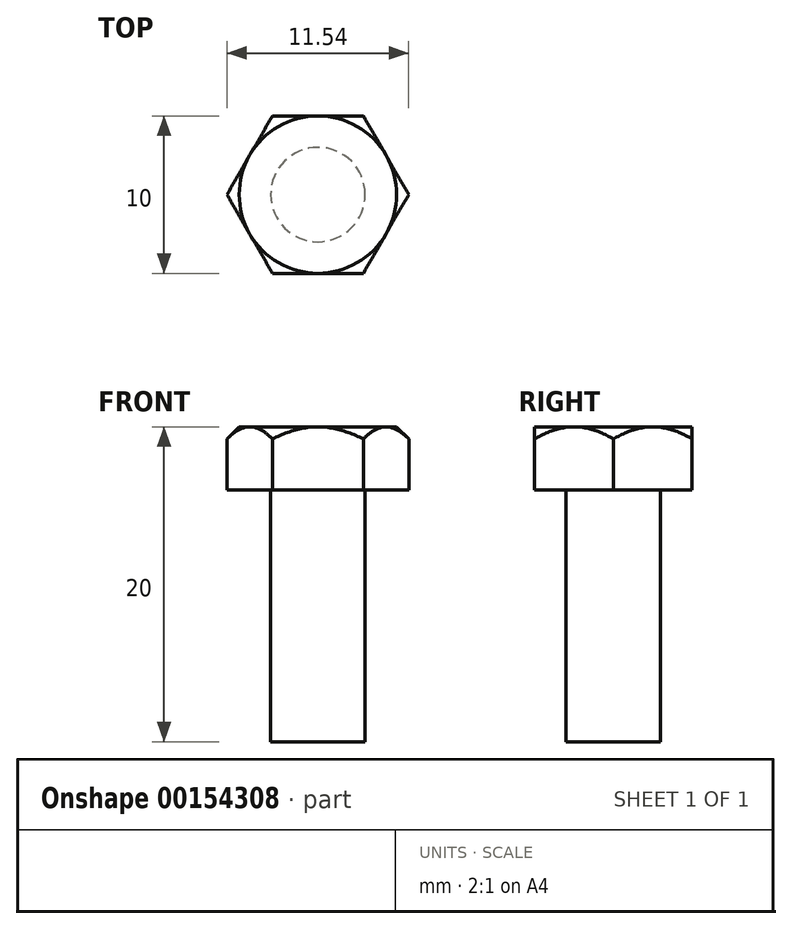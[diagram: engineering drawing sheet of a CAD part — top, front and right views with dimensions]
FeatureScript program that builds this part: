
annotation { "Feature Type Name" : "Feature", "Feature Type Description" : "" }
export const myFeature = defineFeature(function(context is Context, id is Id, definition is map)
    precondition{}
    {
        {
            var Q0;
            Q0=qCreatedBy(makeId("Top.planeOp"),FACE);
            var sketch = newSketch(context, id + "F0", { "sketchPlane" : qUnion([Q0])});
            skCircle(sketch, "E0.cCircle", {"center": v(0, 0) * mm, "radius": 5 * mm, "construction": true});
            skLineSegment(sketch, "E0.0", {"start": v(2.89, -5) * mm, "end": v(-2.89, -5) * mm});
            skLineSegment(sketch, "E0.1", {"start": v(-2.89, -5) * mm, "end": v(-5.77, 0) * mm});
            skLineSegment(sketch, "E0.2", {"start": v(-5.77, 0) * mm, "end": v(-2.89, 5) * mm});
            skLineSegment(sketch, "E0.3", {"start": v(-2.89, 5) * mm, "end": v(2.89, 5) * mm});
            skLineSegment(sketch, "E0.4", {"start": v(2.89, 5) * mm, "end": v(5.77, 0) * mm});
            skLineSegment(sketch, "E0.5", {"start": v(5.77, 0) * mm, "end": v(2.89, -5) * mm});
            skPoint(sketch, "E0.0.midPoint", {"position": v(0, -5) * mm});
            skSolve(sketch);
        }
        {
            var Q0;
            Q0 = qSketchRegion(id + "F0", true);
            extrude(context, id + "F1", {"entities" : qUnion([Q0]), "depth" : 4 * mm});
        }
        {
            var Q0;
            Q0=makeQuery(id+"F1.opExtrude","CAP_FACE",FACE,{"disambiguationData":[OSD([sQuery(id+"F0.wireOp",EDGE,"E0.0"),sQuery(id+"F0.wireOp",EDGE,"E0.1"),sQuery(id+"F0.wireOp",EDGE,"E0.2"),sQuery(id+"F0.wireOp",EDGE,"E0.3"),sQuery(id+"F0.wireOp",EDGE,"E0.4"),sQuery(id+"F0.wireOp",EDGE,"E0.5")])],"isStart":true});
            var sketch = newSketch(context, id + "F2", { "sketchPlane" : qUnion([Q0])});
            skCircle(sketch, "E1", {"center": v(0, 0) * mm, "radius": 3 * mm});
            skSolve(sketch);
        }
        {
            var Q0;
            Q0 = qSketchRegion(id + "F2", true);
            extrude(context, id + "F3", {"entities" : qUnion([Q0]), "operationType" : NewBodyOperationType.ADD, "depth" : 16 * mm});
        }
        {
            var Q0;
            Q0=qCreatedBy(makeId("Right.planeOp"),FACE);
            var sketch = newSketch(context, id + "F4", { "sketchPlane" : qUnion([Q0])});
            skLineSegment(sketch, "E2", {"start": v(5, 4) * mm, "end": v(9, 4) * mm});
            skLineSegment(sketch, "E3", {"start": v(9, 4) * mm, "end": v(9, 0) * mm});
            skLineSegment(sketch, "E4", {"start": v(9, 0) * mm, "end": v(5, 4) * mm});
            skLineSegment(sketch, "E5", {"start": v(0, 0) * mm, "end": v(9, 0) * mm, "construction": true});
            skLineSegment(sketch, "E6", {"start": v(0, 0) * mm, "end": v(0, -2.42) * mm, "construction": true});
            skSolve(sketch);
        }
        {
            var Q0;
            Q0=makeQuery(id+"F4.imprint","IMPRINT",FACE,{"disambiguationData":[TD([[makeQuery(id+"F4.imprint","IMPRINT",EDGE,{"derivedFrom":sQuery(id+"F4.wireOp",EDGE,"E2")}),-1.0]])]});
            var Q1;
            Q1=sQuery(id+"F4.wireOp",EDGE,"E6");
            var Q2;
            Q2=sQuery(id+"F4.wireOp",EDGE,"E6");
            revolve(context, id + "F5", {"operationType" : NewBodyOperationType.REMOVE, "entities" : qUnion([Q0]), "surfaceEntities" : qUnion([Q1]), "axis" : qUnion([Q2]), "revolveType" : RevolveType.FULL, "oppositeDirection" : true});
        }
    });
